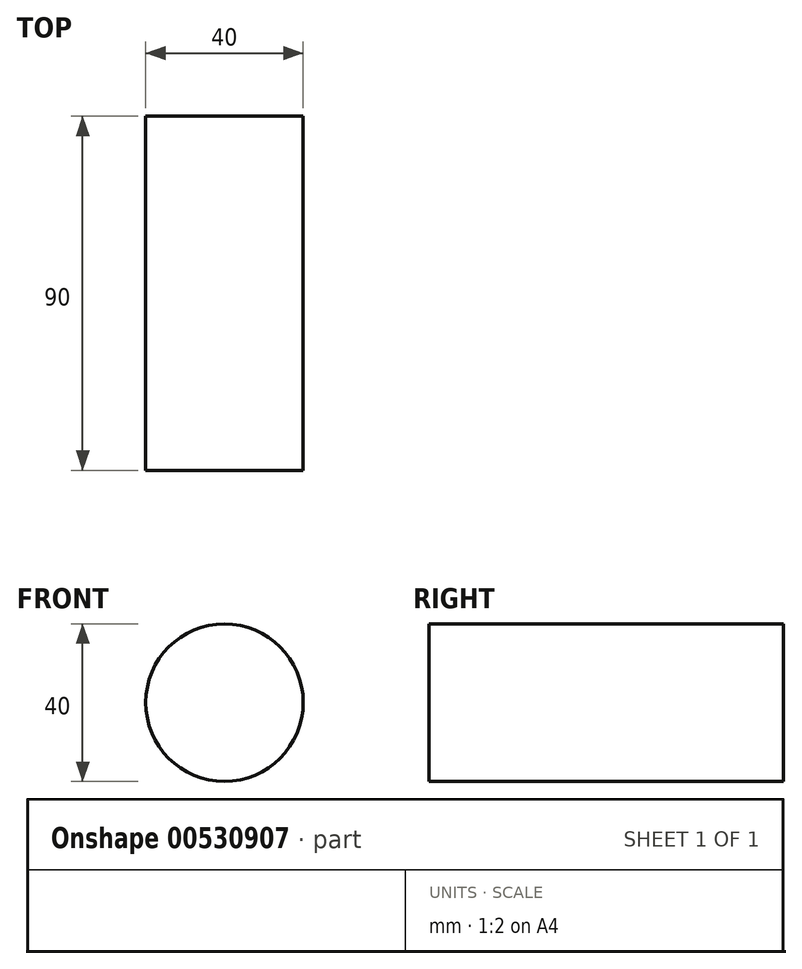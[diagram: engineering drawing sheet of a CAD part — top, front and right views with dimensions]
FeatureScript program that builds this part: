
annotation { "Feature Type Name" : "Feature", "Feature Type Description" : "" }
export const myFeature = defineFeature(function(context is Context, id is Id, definition is map)
    precondition{}
    {
        {
            var Q0;
            Q0=qCreatedBy(makeId("Right.planeOp"),FACE);
            var sketch = newSketch(context, id + "F0", { "sketchPlane" : qUnion([Q0])});
            skLineSegment(sketch, "E0.bottom", {"start": v(-45.52, 20) * mm, "end": v(44.48, 20) * mm});
            skLineSegment(sketch, "E0.top", {"start": v(-45.52, 0) * mm, "end": v(44.48, 0) * mm});
            skLineSegment(sketch, "E0.left", {"start": v(-45.52, 20) * mm, "end": v(-45.52, 0) * mm});
            skLineSegment(sketch, "E0.right", {"start": v(44.48, 20) * mm, "end": v(44.48, 0) * mm});
            skLineSegment(sketch, "E1", {"start": v(-45.22, 0) * mm, "end": v(44.1, 0) * mm, "construction": true});
            skLineSegment(sketch, "E2", {"start": v(-12.83, 20) * mm, "end": v(-20.7, 20) * mm});
            skSolve(sketch);
        }
        {
            var Q0;
            Q0=makeQuery(id+"F0.imprint","IMPRINT",FACE,{"disambiguationData":[TD([[makeQuery(id+"F0.imprint","IMPRINT",EDGE,{"derivedFrom":sQuery(id+"F0.wireOp",EDGE,"E0.top")}),1.0]])]});
            var Q1;
            Q1=sQuery(id+"F0.wireOp",EDGE,"E0.top");
            revolve(context, id + "F1", {"entities" : qUnion([Q0]), "axis" : qUnion([Q1]), "revolveType" : RevolveType.FULL, "oppositeDirection" : true});
        }
    });
